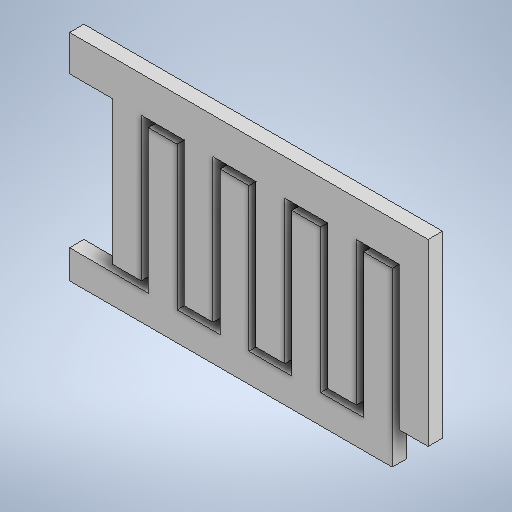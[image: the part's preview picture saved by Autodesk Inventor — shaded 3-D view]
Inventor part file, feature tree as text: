
AUTODESK INVENTOR PART (.ipt)
format: ipt  version: 2025.2 (Build 292293000, 293)  size: 318,464 bytes
history: native  units: mm
features: other x1, extrude x1, sketch x1
ambient origin geometry x8: Origin, YZ Plane, XZ Plane, XY Plane, X Axis, Y Axis, Z Axis, Center Point
bodies: Body1 (feature_tree)
feature tree (3):
  other  "Sólido1"
  extrude  "Extrusão1"  Depth=50.0mm
  sketch  "Esboço1"  dims[d5=5.0mm d6=50.0mm d7=15.0mm d9=25.0mm d10=4.0mm d12=6.0mm d33=2.0mm d34=0.0mm d37=4.0mm d39=15.0mm d43=1.0mm d45=1.0mm d31=0.5mm d32=0.872665mm]
